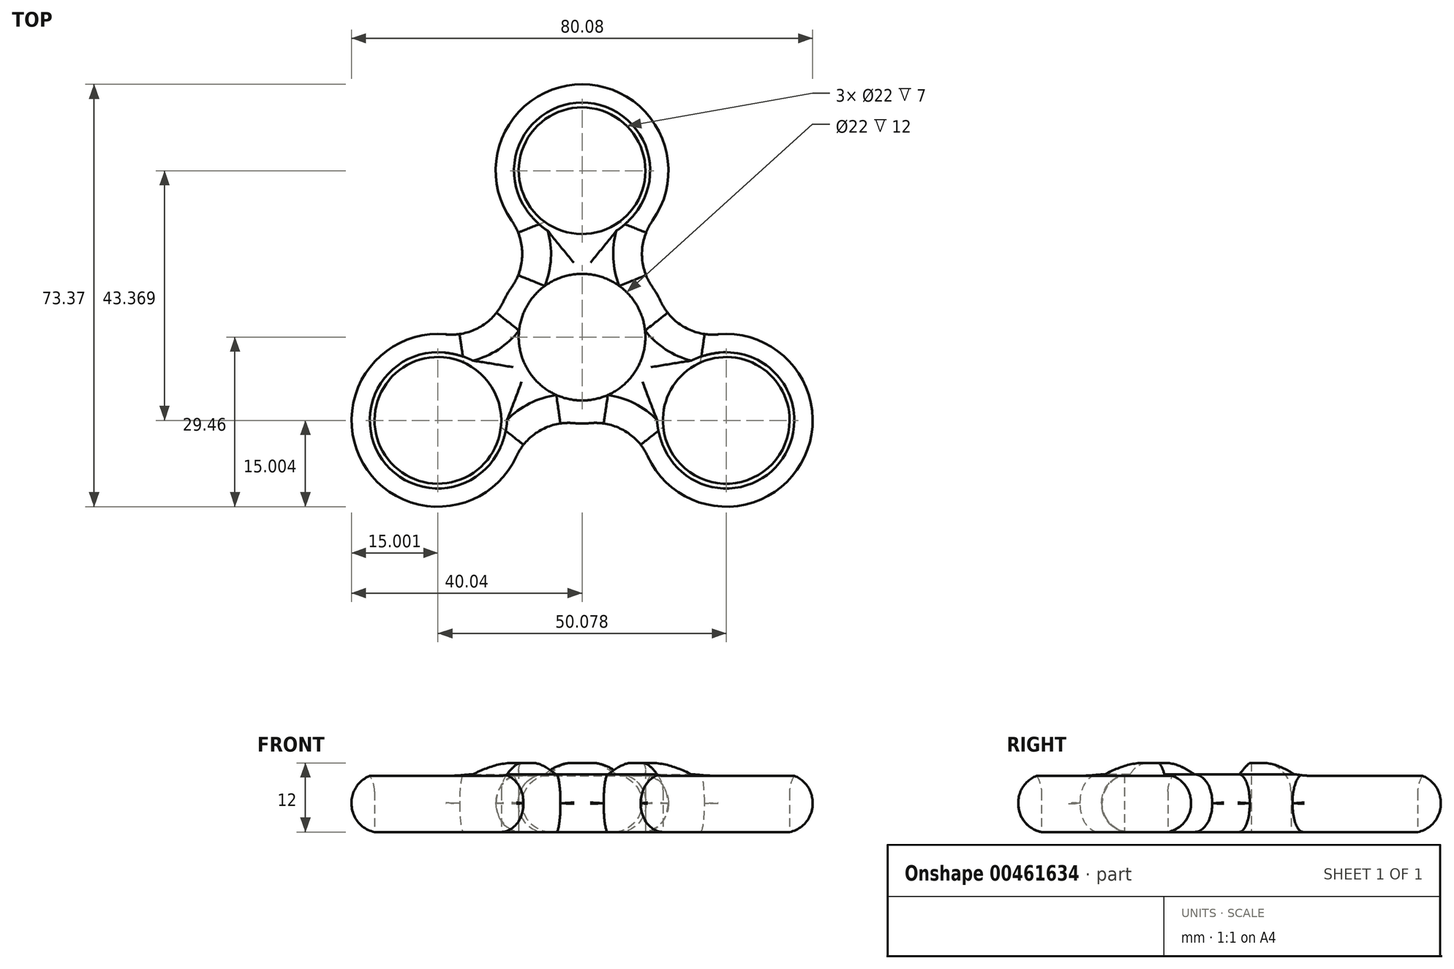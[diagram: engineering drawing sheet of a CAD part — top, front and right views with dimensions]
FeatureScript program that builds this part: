
annotation { "Feature Type Name" : "Feature", "Feature Type Description" : "" }
export const myFeature = defineFeature(function(context is Context, id is Id, definition is map)
    precondition{}
    {
        {
            var Q0;
            Q0=qCreatedBy(makeId("Top.planeOp"),FACE);
            var sketch = newSketch(context, id + "F0", { "sketchPlane" : qUnion([Q0])});
            skCircle(sketch, "E0", {"center": v(0, 0) * mm, "radius": 15 * mm});
            skSolve(sketch);
        }
        {
            var Q0;
            Q0=makeQuery(id+"FH3G6jVPPzJaUqX_0.imprint","IMPRINT",FACE,{"disambiguationData":[TD([[makeQuery(id+"FH3G6jVPPzJaUqX_0.imprint","IMPRINT",EDGE,{"derivedFrom":sQuery(id+"FH3G6jVPPzJaUqX_0.wireOp",EDGE,"1t66u0ux-Mq9E-4tRe-va77-gWhJsKDot20C")}),1.0]])]});
            var Q1;
            Q1=makeQuery(id+"F0.imprint","IMPRINT",FACE,{"disambiguationData":[TD([[makeQuery(id+"F0.imprint","IMPRINT",EDGE,{"derivedFrom":sQuery(id+"F0.wireOp",EDGE,"E0")}),1.0]])]});
            var Q2;
            Q2=makeQuery(id+"FH3G6jVPPzJaUqX_0.imprint","IMPRINT",FACE,{"disambiguationData":[TD([[makeQuery(id+"FH3G6jVPPzJaUqX_0.imprint","IMPRINT",EDGE,{"derivedFrom":sQuery(id+"FH3G6jVPPzJaUqX_0.wireOp",EDGE,"5f4d2418-c4b2-435b-843a-2def000c6f27.2.0")}),1.0]])]});
            var Q3;
            Q3=makeQuery(id+"FH3G6jVPPzJaUqX_0.imprint","IMPRINT",FACE,{"disambiguationData":[TD([[makeQuery(id+"FH3G6jVPPzJaUqX_0.imprint","IMPRINT",EDGE,{"derivedFrom":sQuery(id+"FH3G6jVPPzJaUqX_0.wireOp",EDGE,"5f4d2418-c4b2-435b-843a-2def000c6f27.1.0")}),1.0]])]});
            extrude(context, id + "F1", {"entities" : qUnion([Q0, Q1, Q2, Q3]), "depth" : 10 * mm, "offsetDistance" : 25 * mm});
        }
        {
            var Q0;
            Q0=qCreatedBy(makeId("Top.planeOp"),FACE);
            var sketch = newSketch(context, id + "F2", { "sketchPlane" : qUnion([Q0])});
            skCircle(sketch, "E1", {"center": v(0, 28.91) * mm, "radius": 15 * mm});
            skCircle(sketch, "E2.1.0", {"center": v(-25.04, -14.46) * mm, "radius": 15 * mm});
            skCircle(sketch, "E2.2.0", {"center": v(25.04, -14.46) * mm, "radius": 15 * mm});
            skPoint(sketch, "E2.center", {"position": v(0, 0) * mm});
            skSolve(sketch);
        }
        {
            var Q0;
            Q0=makeQuery(id+"F2.imprint","IMPRINT",FACE,{"disambiguationData":[TD([[makeQuery(id+"F2.imprint","IMPRINT",EDGE,{"derivedFrom":sQuery(id+"F2.wireOp",EDGE,"E1")}),1.0]])]});
            var Q1;
            Q1=makeQuery(id+"F2.imprint","IMPRINT",FACE,{"disambiguationData":[TD([[makeQuery(id+"F2.imprint","IMPRINT",EDGE,{"derivedFrom":sQuery(id+"F2.wireOp",EDGE,"E2.2.0")}),1.0]])]});
            var Q2;
            Q2=makeQuery(id+"F2.imprint","IMPRINT",FACE,{"disambiguationData":[TD([[makeQuery(id+"F2.imprint","IMPRINT",EDGE,{"derivedFrom":sQuery(id+"F2.wireOp",EDGE,"E2.1.0")}),1.0]])]});
            extrude(context, id + "F3", {"entities" : qUnion([Q0, Q1, Q2]), "operationType" : NewBodyOperationType.ADD, "depth" : 10 * mm, "offsetDistance" : 25 * mm});
        }
        {
            var Q0;
            Q0=makeQuery(id+"F3.boolean.opBoolean","MERGE",FACE,{"derivedFrom":[makeQuery(id+"F1.opExtrude","CAP_FACE",FACE,{"disambiguationData":[OSD([sQuery(id+"F0.wireOp",EDGE,"E0")])],"isStart":true}),makeQuery(id+"F3.opExtrude","CAP_FACE",FACE,{"disambiguationData":[OSD([sQuery(id+"F2.wireOp",EDGE,"E1")])],"isStart":true}),makeQuery(id+"F3.opExtrude","CAP_FACE",FACE,{"disambiguationData":[OSD([sQuery(id+"F2.wireOp",EDGE,"E2.1.0")])],"isStart":true}),makeQuery(id+"F3.opExtrude","CAP_FACE",FACE,{"disambiguationData":[OSD([sQuery(id+"F2.wireOp",EDGE,"E2.2.0")])],"isStart":true})]});
            var sketch = newSketch(context, id + "F4", { "sketchPlane" : qUnion([Q0])});
            skCircle(sketch, "E3", {"center": v(0, -28.91) * mm, "radius": 11 * mm});
            skSolve(sketch);
        }
        {
            var Q0;
            Q0=makeQuery(id+"F4.imprint","IMPRINT",FACE,{"disambiguationData":[TD([[makeQuery(id+"F4.imprint","IMPRINT",EDGE,{"derivedFrom":sQuery(id+"F4.wireOp",EDGE,"E3")}),-1.0]])]});
            var sketch = newSketch(context, id + "F5", { "sketchPlane" : qUnion([Q0])});
            skCircle(sketch, "E4", {"center": v(0, 0) * mm, "radius": 11 * mm});
            skSolve(sketch);
        }
        {
            var Q0;
            Q0=makeQuery(id+"F4.imprint","IMPRINT",FACE,{"disambiguationData":[TD([[makeQuery(id+"F4.imprint","IMPRINT",EDGE,{"derivedFrom":sQuery(id+"F4.wireOp",EDGE,"E3")}),1.0]])]});
            extrude(context, id + "F6", {"entities" : qUnion([Q0]), "operationType" : NewBodyOperationType.REMOVE, "oppositeDirection" : true, "depth" : 25 * mm, "offsetDistance" : 25 * mm});
        }
        {
            var Q0;
            Q0=makeQuery(id+"F5.imprint","IMPRINT",FACE,{"disambiguationData":[TD([[makeQuery(id+"F5.imprint","IMPRINT",EDGE,{"derivedFrom":sQuery(id+"F5.wireOp",EDGE,"E4")}),1.0]])]});
            extrude(context, id + "F7", {"entities" : qUnion([Q0]), "operationType" : NewBodyOperationType.REMOVE, "oppositeDirection" : true, "depth" : 25 * mm, "offsetDistance" : 25 * mm});
        }
        {
            var Q0;
            Q0=makeQuery(id+"F3.boolean.opBoolean","MERGE",FACE,{"derivedFrom":[makeQuery(id+"F1.opExtrude","CAP_FACE",FACE,{"disambiguationData":[OSD([sQuery(id+"F0.wireOp",EDGE,"E0")])],"isStart":true}),makeQuery(id+"F3.opExtrude","CAP_FACE",FACE,{"disambiguationData":[OSD([sQuery(id+"F2.wireOp",EDGE,"E1")])],"isStart":true}),makeQuery(id+"F3.opExtrude","CAP_FACE",FACE,{"disambiguationData":[OSD([sQuery(id+"F2.wireOp",EDGE,"E2.1.0")])],"isStart":true}),makeQuery(id+"F3.opExtrude","CAP_FACE",FACE,{"disambiguationData":[OSD([sQuery(id+"F2.wireOp",EDGE,"E2.2.0")])],"isStart":true})]});
            var sketch = newSketch(context, id + "F8", { "sketchPlane" : qUnion([Q0])});
            skCircle(sketch, "E5", {"center": v(-25.04, 14.46) * mm, "radius": 11 * mm});
            skSolve(sketch);
        }
        {
            var Q0;
            Q0=makeQuery(id+"F8.imprint","IMPRINT",FACE,{"disambiguationData":[TD([[makeQuery(id+"F8.imprint","IMPRINT",EDGE,{"derivedFrom":sQuery(id+"F8.wireOp",EDGE,"E5")}),1.0]])]});
            extrude(context, id + "F9", {"entities" : qUnion([Q0]), "operationType" : NewBodyOperationType.REMOVE, "oppositeDirection" : true, "depth" : 25 * mm, "offsetDistance" : 25 * mm});
        }
        {
            var Q0;
            Q0=makeQuery(id+"F3.boolean.opBoolean","MERGE",FACE,{"derivedFrom":[makeQuery(id+"F1.opExtrude","CAP_FACE",FACE,{"disambiguationData":[OSD([sQuery(id+"F0.wireOp",EDGE,"E0")])],"isStart":true}),makeQuery(id+"F3.opExtrude","CAP_FACE",FACE,{"disambiguationData":[OSD([sQuery(id+"F2.wireOp",EDGE,"E1")])],"isStart":true}),makeQuery(id+"F3.opExtrude","CAP_FACE",FACE,{"disambiguationData":[OSD([sQuery(id+"F2.wireOp",EDGE,"E2.1.0")])],"isStart":true}),makeQuery(id+"F3.opExtrude","CAP_FACE",FACE,{"disambiguationData":[OSD([sQuery(id+"F2.wireOp",EDGE,"E2.2.0")])],"isStart":true})]});
            var sketch = newSketch(context, id + "F10", { "sketchPlane" : qUnion([Q0])});
            skCircle(sketch, "E6", {"center": v(25.04, 14.46) * mm, "radius": 11 * mm});
            skSolve(sketch);
        }
        {
            var Q0;
            Q0=makeQuery(id+"F10.imprint","IMPRINT",FACE,{"disambiguationData":[TD([[makeQuery(id+"F10.imprint","IMPRINT",EDGE,{"derivedFrom":sQuery(id+"F10.wireOp",EDGE,"E6")}),1.0]])]});
            extrude(context, id + "F11", {"entities" : qUnion([Q0]), "operationType" : NewBodyOperationType.REMOVE, "oppositeDirection" : true, "depth" : 25 * mm, "offsetDistance" : 25 * mm});
        }
        {
            var Q0;
            Q0=makeQuery(id+"F3.boolean.opBoolean","INTERSECT",EDGE,{"disambiguationData":[OD(1.0)],"derivedFrom":[makeQuery(id+"F1.opExtrude","SWEPT_FACE",FACE,{"disambiguationData":[OSD([sQuery(id+"F0.wireOp",EDGE,"E0")])]}),makeQuery(id+"F3.opExtrude","SWEPT_FACE",FACE,{"disambiguationData":[OSD([sQuery(id+"F2.wireOp",EDGE,"E2.2.0")])]})]});
            var Q1;
            Q1=makeQuery(id+"F3.boolean.opBoolean","INTERSECT",EDGE,{"disambiguationData":[OD(1.0)],"derivedFrom":[makeQuery(id+"F1.opExtrude","SWEPT_FACE",FACE,{"disambiguationData":[OSD([sQuery(id+"F0.wireOp",EDGE,"E0")])]}),makeQuery(id+"F3.opExtrude","SWEPT_FACE",FACE,{"disambiguationData":[OSD([sQuery(id+"F2.wireOp",EDGE,"E2.1.0")])]})]});
            var Q2;
            Q2=makeQuery(id+"F3.boolean.opBoolean","INTERSECT",EDGE,{"disambiguationData":[OD(0.0)],"derivedFrom":[makeQuery(id+"F1.opExtrude","SWEPT_FACE",FACE,{"disambiguationData":[OSD([sQuery(id+"F0.wireOp",EDGE,"E0")])]}),makeQuery(id+"F3.opExtrude","SWEPT_FACE",FACE,{"disambiguationData":[OSD([sQuery(id+"F2.wireOp",EDGE,"E2.1.0")])]})]});
            var Q3;
            Q3=makeQuery(id+"F3.boolean.opBoolean","INTERSECT",EDGE,{"disambiguationData":[OD(0.0)],"derivedFrom":[makeQuery(id+"F1.opExtrude","SWEPT_FACE",FACE,{"disambiguationData":[OSD([sQuery(id+"F0.wireOp",EDGE,"E0")])]}),makeQuery(id+"F3.opExtrude","SWEPT_FACE",FACE,{"disambiguationData":[OSD([sQuery(id+"F2.wireOp",EDGE,"E1")])]})]});
            var Q4;
            Q4=makeQuery(id+"F3.boolean.opBoolean","INTERSECT",EDGE,{"disambiguationData":[OD(1.0)],"derivedFrom":[makeQuery(id+"F1.opExtrude","SWEPT_FACE",FACE,{"disambiguationData":[OSD([sQuery(id+"F0.wireOp",EDGE,"E0")])]}),makeQuery(id+"F3.opExtrude","SWEPT_FACE",FACE,{"disambiguationData":[OSD([sQuery(id+"F2.wireOp",EDGE,"E1")])]})]});
            var Q5;
            Q5=makeQuery(id+"F3.boolean.opBoolean","INTERSECT",EDGE,{"disambiguationData":[OD(0.0)],"derivedFrom":[makeQuery(id+"F1.opExtrude","SWEPT_FACE",FACE,{"disambiguationData":[OSD([sQuery(id+"F0.wireOp",EDGE,"E0")])]}),makeQuery(id+"F3.opExtrude","SWEPT_FACE",FACE,{"disambiguationData":[OSD([sQuery(id+"F2.wireOp",EDGE,"E2.2.0")])]})]});
            fillet(context, id + "F12", {"entities" : qUnion([Q0, Q1, Q2, Q3, Q4, Q5]), "radius" : 10 * mm, "tangentPropagation" : true, "allowEdgeOverflow" : false});
        }
        {
            var Q0;
            Q0=makeQuery(id+"F3.opExtrude","CAP_EDGE",EDGE,{"disambiguationData":[OSD([sQuery(id+"F2.wireOp",EDGE,"E2.1.0")])],"isStart":true});
            var Q1;
            Q1=makeQuery(id+"F3.opExtrude","CAP_EDGE",EDGE,{"disambiguationData":[OSD([sQuery(id+"F2.wireOp",EDGE,"E1")])],"isStart":false});
            fillet(context, id + "F13", {"entities" : qUnion([Q0, Q1]), "radius" : 5 * mm, "tangentPropagation" : true, "allowEdgeOverflow" : false});
        }
        {
            var Q0;
            Q0=makeQuery(id+"F13.opFillet","SPLIT",FACE,{"disambiguationData":[OD(2.0)],"derivedFrom":makeQuery(id+"F3.boolean.opBoolean","MERGE",FACE,{"derivedFrom":[makeQuery(id+"F1.opExtrude","CAP_FACE",FACE,{"disambiguationData":[OSD([sQuery(id+"F0.wireOp",EDGE,"E0")])],"isStart":false}),makeQuery(id+"F3.opExtrude","CAP_FACE",FACE,{"disambiguationData":[OSD([sQuery(id+"F2.wireOp",EDGE,"E1")])],"isStart":false}),makeQuery(id+"F3.opExtrude","CAP_FACE",FACE,{"disambiguationData":[OSD([sQuery(id+"F2.wireOp",EDGE,"E2.1.0")])],"isStart":false}),makeQuery(id+"F3.opExtrude","CAP_FACE",FACE,{"disambiguationData":[OSD([sQuery(id+"F2.wireOp",EDGE,"E2.2.0")])],"isStart":false})]})});
            extrude(context, id + "F14", {"entities" : qUnion([Q0]), "operationType" : NewBodyOperationType.ADD, "depth" : 2 * mm, "offsetDistance" : 25 * mm});
        }
        {
            var Q0;
            Q0=makeQuery(id+"F13.opFillet","SPLIT",FACE,{"disambiguationData":[OD(0.0)],"derivedFrom":makeQuery(id+"F3.boolean.opBoolean","MERGE",FACE,{"derivedFrom":[makeQuery(id+"F1.opExtrude","CAP_FACE",FACE,{"disambiguationData":[OSD([sQuery(id+"F0.wireOp",EDGE,"E0")])],"isStart":false}),makeQuery(id+"F3.opExtrude","CAP_FACE",FACE,{"disambiguationData":[OSD([sQuery(id+"F2.wireOp",EDGE,"E1")])],"isStart":false}),makeQuery(id+"F3.opExtrude","CAP_FACE",FACE,{"disambiguationData":[OSD([sQuery(id+"F2.wireOp",EDGE,"E2.1.0")])],"isStart":false}),makeQuery(id+"F3.opExtrude","CAP_FACE",FACE,{"disambiguationData":[OSD([sQuery(id+"F2.wireOp",EDGE,"E2.2.0")])],"isStart":false})]})});
            var Q1;
            Q1=makeQuery(id+"F13.opFillet","SPLIT",FACE,{"disambiguationData":[OD(1.0)],"derivedFrom":makeQuery(id+"F3.boolean.opBoolean","MERGE",FACE,{"derivedFrom":[makeQuery(id+"F1.opExtrude","CAP_FACE",FACE,{"disambiguationData":[OSD([sQuery(id+"F0.wireOp",EDGE,"E0")])],"isStart":false}),makeQuery(id+"F3.opExtrude","CAP_FACE",FACE,{"disambiguationData":[OSD([sQuery(id+"F2.wireOp",EDGE,"E1")])],"isStart":false}),makeQuery(id+"F3.opExtrude","CAP_FACE",FACE,{"disambiguationData":[OSD([sQuery(id+"F2.wireOp",EDGE,"E2.1.0")])],"isStart":false}),makeQuery(id+"F3.opExtrude","CAP_FACE",FACE,{"disambiguationData":[OSD([sQuery(id+"F2.wireOp",EDGE,"E2.2.0")])],"isStart":false})]})});
            extrude(context, id + "F15", {"entities" : qUnion([Q0, Q1]), "operationType" : NewBodyOperationType.ADD, "depth" : 2 * mm, "offsetDistance" : 25 * mm});
        }
        {
            var Q0;
            Q0=makeQuery(id+"F15.opExtrude","CAP_EDGE",EDGE,{"disambiguationData":[OSD([sQuery(id+"F0.wireOp",EDGE,"E0"),sQuery(id+"F2.wireOp",EDGE,"E1"),sQuery(id+"F2.wireOp",EDGE,"E2.1.0"),sQuery(id+"F2.wireOp",EDGE,"E2.2.0"),sQuery(id+"F8.wireOp",EDGE,"E5")])],"isStart":false});
            var Q1;
            Q1=makeQuery(id+"F14.opExtrude","CAP_EDGE",EDGE,{"disambiguationData":[OSD([sQuery(id+"F0.wireOp",EDGE,"E0"),sQuery(id+"F2.wireOp",EDGE,"E1"),sQuery(id+"F2.wireOp",EDGE,"E2.1.0"),sQuery(id+"F2.wireOp",EDGE,"E2.2.0"),sQuery(id+"F10.wireOp",EDGE,"E6")])],"isStart":false});
            var Q2;
            Q2=makeQuery(id+"F15.opExtrude","CAP_EDGE",EDGE,{"disambiguationData":[OSD([sQuery(id+"F0.wireOp",EDGE,"E0"),sQuery(id+"F2.wireOp",EDGE,"E1"),sQuery(id+"F2.wireOp",EDGE,"E2.1.0"),sQuery(id+"F2.wireOp",EDGE,"E2.2.0"),sQuery(id+"F4.wireOp",EDGE,"E3")])],"isStart":false});
            fillet(context, id + "F16", {"entities" : qUnion([Q0, Q1, Q2]), "radius" : 5 * mm, "tangentPropagation" : true, "allowEdgeOverflow" : false});
        }
        {
            var Q0;
            {var subQ0=sQuery(id+"F2.wireOp",EDGE,"E2.2.0");var subQ1=sQuery(id+"F2.wireOp",EDGE,"E2.1.0");var subQ2=sQuery(id+"F2.wireOp",EDGE,"E1");var subQ3=sQuery(id+"F0.wireOp",EDGE,"E0");var subQ4=makeQuery(id+"F3.boolean.opBoolean","MERGE",FACE,{"derivedFrom":[makeQuery(id+"F1.opExtrude","CAP_FACE",FACE,{"disambiguationData":[OSD([subQ3])],"isStart":false}),makeQuery(id+"F3.opExtrude","CAP_FACE",FACE,{"disambiguationData":[OSD([subQ2])],"isStart":false}),makeQuery(id+"F3.opExtrude","CAP_FACE",FACE,{"disambiguationData":[OSD([subQ1])],"isStart":false}),makeQuery(id+"F3.opExtrude","CAP_FACE",FACE,{"disambiguationData":[OSD([subQ0])],"isStart":false})]});Q0=makeQuery(id+"F16.opFillet","BLEND_EDGE",EDGE,{"blendedFrom":[makeQuery(id+"F15.opExtrude","CAP_EDGE",EDGE,{"disambiguationData":[OSD([subQ3,subQ2,subQ1,subQ0,sQuery(id+"F8.wireOp",EDGE,"E5")])],"isStart":false}),makeQuery(id+"F15.opExtrude","SWEPT_FACE",FACE,{"disambiguationData":[OSD([subQ3,subQ2,subQ1,subQ0]),TDD([makeQuery(id+"F13.opFillet","BLEND_EDGE",EDGE,{"blendedFrom":[makeQuery(id+"F12.opFillet","BLEND_EDGE",EDGE,{"blendedFrom":[makeQuery(id+"F3.boolean.opBoolean","INTERSECT",EDGE,{"disambiguationData":[OD(0.0)],"derivedFrom":[makeQuery(id+"F1.opExtrude","SWEPT_FACE",FACE,{"disambiguationData":[OSD([subQ3])]}),makeQuery(id+"F3.opExtrude","SWEPT_FACE",FACE,{"disambiguationData":[OSD([subQ1])]})]}),subQ4],"blendedInto":[subQ4]}),subQ4],"blendedInto":[subQ4]})])]})],"blendedInto":[makeQuery(id+"F15.opExtrude","SWEPT_FACE",FACE,{"disambiguationData":[OSD([subQ3,subQ2,subQ1,subQ0]),TDD([makeQuery(id+"F13.opFillet","BLEND_EDGE",EDGE,{"blendedFrom":[makeQuery(id+"F12.opFillet","BLEND_EDGE",EDGE,{"blendedFrom":[makeQuery(id+"F3.boolean.opBoolean","INTERSECT",EDGE,{"disambiguationData":[OD(0.0)],"derivedFrom":[makeQuery(id+"F1.opExtrude","SWEPT_FACE",FACE,{"disambiguationData":[OSD([subQ3])]}),makeQuery(id+"F3.opExtrude","SWEPT_FACE",FACE,{"disambiguationData":[OSD([subQ1])]})]}),subQ4],"blendedInto":[subQ4]}),subQ4],"blendedInto":[subQ4]})])]})]});}
            fillet(context, id + "F17", {"entities" : qUnion([Q0]), "radius" : 5 * mm, "tangentPropagation" : true, "allowEdgeOverflow" : false});
        }
        {
            var Q0;
            {var subQ0=sQuery(id+"F2.wireOp",EDGE,"E2.2.0");var subQ1=sQuery(id+"F2.wireOp",EDGE,"E2.1.0");var subQ2=sQuery(id+"F2.wireOp",EDGE,"E1");var subQ3=sQuery(id+"F0.wireOp",EDGE,"E0");var subQ4=makeQuery(id+"F3.boolean.opBoolean","MERGE",FACE,{"derivedFrom":[makeQuery(id+"F1.opExtrude","CAP_FACE",FACE,{"disambiguationData":[OSD([subQ3])],"isStart":false}),makeQuery(id+"F3.opExtrude","CAP_FACE",FACE,{"disambiguationData":[OSD([subQ2])],"isStart":false}),makeQuery(id+"F3.opExtrude","CAP_FACE",FACE,{"disambiguationData":[OSD([subQ1])],"isStart":false}),makeQuery(id+"F3.opExtrude","CAP_FACE",FACE,{"disambiguationData":[OSD([subQ0])],"isStart":false})]});Q0=makeQuery(id+"F16.opFillet","BLEND_EDGE",EDGE,{"blendedFrom":[makeQuery(id+"F15.opExtrude","CAP_EDGE",EDGE,{"disambiguationData":[OSD([subQ3,subQ2,subQ1,subQ0,sQuery(id+"F8.wireOp",EDGE,"E5")])],"isStart":false}),makeQuery(id+"F15.opExtrude","SWEPT_FACE",FACE,{"disambiguationData":[OSD([subQ3,subQ2,subQ1,subQ0]),TDD([makeQuery(id+"F13.opFillet","BLEND_EDGE",EDGE,{"blendedFrom":[makeQuery(id+"F12.opFillet","BLEND_EDGE",EDGE,{"blendedFrom":[makeQuery(id+"F3.boolean.opBoolean","INTERSECT",EDGE,{"disambiguationData":[OD(1.0)],"derivedFrom":[makeQuery(id+"F1.opExtrude","SWEPT_FACE",FACE,{"disambiguationData":[OSD([subQ3])]}),makeQuery(id+"F3.opExtrude","SWEPT_FACE",FACE,{"disambiguationData":[OSD([subQ1])]})]}),subQ4],"blendedInto":[subQ4]}),subQ4],"blendedInto":[subQ4]})])]})],"blendedInto":[makeQuery(id+"F15.opExtrude","SWEPT_FACE",FACE,{"disambiguationData":[OSD([subQ3,subQ2,subQ1,subQ0]),TDD([makeQuery(id+"F13.opFillet","BLEND_EDGE",EDGE,{"blendedFrom":[makeQuery(id+"F12.opFillet","BLEND_EDGE",EDGE,{"blendedFrom":[makeQuery(id+"F3.boolean.opBoolean","INTERSECT",EDGE,{"disambiguationData":[OD(1.0)],"derivedFrom":[makeQuery(id+"F1.opExtrude","SWEPT_FACE",FACE,{"disambiguationData":[OSD([subQ3])]}),makeQuery(id+"F3.opExtrude","SWEPT_FACE",FACE,{"disambiguationData":[OSD([subQ1])]})]}),subQ4],"blendedInto":[subQ4]}),subQ4],"blendedInto":[subQ4]})])]})]});}
            fillet(context, id + "F18", {"entities" : qUnion([Q0]), "radius" : 5 * mm, "tangentPropagation" : true, "allowEdgeOverflow" : false});
        }
        {
            var Q0;
            {var subQ0=sQuery(id+"F2.wireOp",EDGE,"E2.2.0");var subQ1=sQuery(id+"F2.wireOp",EDGE,"E2.1.0");var subQ2=sQuery(id+"F2.wireOp",EDGE,"E1");var subQ3=sQuery(id+"F0.wireOp",EDGE,"E0");var subQ4=makeQuery(id+"F3.boolean.opBoolean","MERGE",FACE,{"derivedFrom":[makeQuery(id+"F1.opExtrude","CAP_FACE",FACE,{"disambiguationData":[OSD([subQ3])],"isStart":false}),makeQuery(id+"F3.opExtrude","CAP_FACE",FACE,{"disambiguationData":[OSD([subQ2])],"isStart":false}),makeQuery(id+"F3.opExtrude","CAP_FACE",FACE,{"disambiguationData":[OSD([subQ1])],"isStart":false}),makeQuery(id+"F3.opExtrude","CAP_FACE",FACE,{"disambiguationData":[OSD([subQ0])],"isStart":false})]});Q0=makeQuery(id+"F16.opFillet","BLEND_EDGE",EDGE,{"blendedFrom":[makeQuery(id+"F14.opExtrude","CAP_EDGE",EDGE,{"disambiguationData":[OSD([subQ3,subQ2,subQ1,subQ0,sQuery(id+"F10.wireOp",EDGE,"E6")])],"isStart":false}),makeQuery(id+"F14.opExtrude","SWEPT_FACE",FACE,{"disambiguationData":[OSD([subQ3,subQ2,subQ1,subQ0]),TDD([makeQuery(id+"F13.opFillet","BLEND_EDGE",EDGE,{"blendedFrom":[makeQuery(id+"F12.opFillet","BLEND_EDGE",EDGE,{"blendedFrom":[makeQuery(id+"F3.boolean.opBoolean","INTERSECT",EDGE,{"disambiguationData":[OD(0.0)],"derivedFrom":[makeQuery(id+"F1.opExtrude","SWEPT_FACE",FACE,{"disambiguationData":[OSD([subQ3])]}),makeQuery(id+"F3.opExtrude","SWEPT_FACE",FACE,{"disambiguationData":[OSD([subQ0])]})]}),subQ4],"blendedInto":[subQ4]}),subQ4],"blendedInto":[subQ4]})])]})],"blendedInto":[makeQuery(id+"F14.opExtrude","SWEPT_FACE",FACE,{"disambiguationData":[OSD([subQ3,subQ2,subQ1,subQ0]),TDD([makeQuery(id+"F13.opFillet","BLEND_EDGE",EDGE,{"blendedFrom":[makeQuery(id+"F12.opFillet","BLEND_EDGE",EDGE,{"blendedFrom":[makeQuery(id+"F3.boolean.opBoolean","INTERSECT",EDGE,{"disambiguationData":[OD(0.0)],"derivedFrom":[makeQuery(id+"F1.opExtrude","SWEPT_FACE",FACE,{"disambiguationData":[OSD([subQ3])]}),makeQuery(id+"F3.opExtrude","SWEPT_FACE",FACE,{"disambiguationData":[OSD([subQ0])]})]}),subQ4],"blendedInto":[subQ4]}),subQ4],"blendedInto":[subQ4]})])]})]});}
            fillet(context, id + "F19", {"entities" : qUnion([Q0]), "radius" : 5 * mm, "tangentPropagation" : true, "allowEdgeOverflow" : false});
        }
        {
            var Q0;
            {var subQ0=sQuery(id+"F2.wireOp",EDGE,"E2.2.0");var subQ1=sQuery(id+"F2.wireOp",EDGE,"E2.1.0");var subQ2=sQuery(id+"F2.wireOp",EDGE,"E1");var subQ3=sQuery(id+"F0.wireOp",EDGE,"E0");var subQ4=makeQuery(id+"F3.boolean.opBoolean","MERGE",FACE,{"derivedFrom":[makeQuery(id+"F1.opExtrude","CAP_FACE",FACE,{"disambiguationData":[OSD([subQ3])],"isStart":false}),makeQuery(id+"F3.opExtrude","CAP_FACE",FACE,{"disambiguationData":[OSD([subQ2])],"isStart":false}),makeQuery(id+"F3.opExtrude","CAP_FACE",FACE,{"disambiguationData":[OSD([subQ1])],"isStart":false}),makeQuery(id+"F3.opExtrude","CAP_FACE",FACE,{"disambiguationData":[OSD([subQ0])],"isStart":false})]});Q0=makeQuery(id+"F16.opFillet","BLEND_EDGE",EDGE,{"blendedFrom":[makeQuery(id+"F14.opExtrude","CAP_EDGE",EDGE,{"disambiguationData":[OSD([subQ3,subQ2,subQ1,subQ0,sQuery(id+"F10.wireOp",EDGE,"E6")])],"isStart":false}),makeQuery(id+"F14.opExtrude","SWEPT_FACE",FACE,{"disambiguationData":[OSD([subQ3,subQ2,subQ1,subQ0]),TDD([makeQuery(id+"F13.opFillet","BLEND_EDGE",EDGE,{"blendedFrom":[makeQuery(id+"F12.opFillet","BLEND_EDGE",EDGE,{"blendedFrom":[makeQuery(id+"F3.boolean.opBoolean","INTERSECT",EDGE,{"disambiguationData":[OD(1.0)],"derivedFrom":[makeQuery(id+"F1.opExtrude","SWEPT_FACE",FACE,{"disambiguationData":[OSD([subQ3])]}),makeQuery(id+"F3.opExtrude","SWEPT_FACE",FACE,{"disambiguationData":[OSD([subQ0])]})]}),subQ4],"blendedInto":[subQ4]}),subQ4],"blendedInto":[subQ4]})])]})],"blendedInto":[makeQuery(id+"F14.opExtrude","SWEPT_FACE",FACE,{"disambiguationData":[OSD([subQ3,subQ2,subQ1,subQ0]),TDD([makeQuery(id+"F13.opFillet","BLEND_EDGE",EDGE,{"blendedFrom":[makeQuery(id+"F12.opFillet","BLEND_EDGE",EDGE,{"blendedFrom":[makeQuery(id+"F3.boolean.opBoolean","INTERSECT",EDGE,{"disambiguationData":[OD(1.0)],"derivedFrom":[makeQuery(id+"F1.opExtrude","SWEPT_FACE",FACE,{"disambiguationData":[OSD([subQ3])]}),makeQuery(id+"F3.opExtrude","SWEPT_FACE",FACE,{"disambiguationData":[OSD([subQ0])]})]}),subQ4],"blendedInto":[subQ4]}),subQ4],"blendedInto":[subQ4]})])]})]});}
            fillet(context, id + "F20", {"entities" : qUnion([Q0]), "radius" : 5 * mm, "tangentPropagation" : true, "allowEdgeOverflow" : false});
        }
        {
            var Q0;
            {var subQ0=sQuery(id+"F2.wireOp",EDGE,"E2.2.0");var subQ1=sQuery(id+"F2.wireOp",EDGE,"E2.1.0");var subQ2=sQuery(id+"F2.wireOp",EDGE,"E1");var subQ3=sQuery(id+"F0.wireOp",EDGE,"E0");var subQ4=makeQuery(id+"F3.boolean.opBoolean","MERGE",FACE,{"derivedFrom":[makeQuery(id+"F1.opExtrude","CAP_FACE",FACE,{"disambiguationData":[OSD([subQ3])],"isStart":false}),makeQuery(id+"F3.opExtrude","CAP_FACE",FACE,{"disambiguationData":[OSD([subQ2])],"isStart":false}),makeQuery(id+"F3.opExtrude","CAP_FACE",FACE,{"disambiguationData":[OSD([subQ1])],"isStart":false}),makeQuery(id+"F3.opExtrude","CAP_FACE",FACE,{"disambiguationData":[OSD([subQ0])],"isStart":false})]});Q0=makeQuery(id+"F16.opFillet","BLEND_EDGE",EDGE,{"blendedFrom":[makeQuery(id+"F15.opExtrude","CAP_EDGE",EDGE,{"disambiguationData":[OSD([subQ3,subQ2,subQ1,subQ0,sQuery(id+"F4.wireOp",EDGE,"E3")])],"isStart":false}),makeQuery(id+"F15.opExtrude","SWEPT_FACE",FACE,{"disambiguationData":[OSD([subQ3,subQ2,subQ1,subQ0]),TDD([makeQuery(id+"F13.opFillet","BLEND_EDGE",EDGE,{"blendedFrom":[makeQuery(id+"F12.opFillet","BLEND_EDGE",EDGE,{"blendedFrom":[makeQuery(id+"F3.boolean.opBoolean","INTERSECT",EDGE,{"disambiguationData":[OD(0.0)],"derivedFrom":[makeQuery(id+"F1.opExtrude","SWEPT_FACE",FACE,{"disambiguationData":[OSD([subQ3])]}),makeQuery(id+"F3.opExtrude","SWEPT_FACE",FACE,{"disambiguationData":[OSD([subQ2])]})]}),subQ4],"blendedInto":[subQ4]}),subQ4],"blendedInto":[subQ4]})])]})],"blendedInto":[makeQuery(id+"F15.opExtrude","SWEPT_FACE",FACE,{"disambiguationData":[OSD([subQ3,subQ2,subQ1,subQ0]),TDD([makeQuery(id+"F13.opFillet","BLEND_EDGE",EDGE,{"blendedFrom":[makeQuery(id+"F12.opFillet","BLEND_EDGE",EDGE,{"blendedFrom":[makeQuery(id+"F3.boolean.opBoolean","INTERSECT",EDGE,{"disambiguationData":[OD(0.0)],"derivedFrom":[makeQuery(id+"F1.opExtrude","SWEPT_FACE",FACE,{"disambiguationData":[OSD([subQ3])]}),makeQuery(id+"F3.opExtrude","SWEPT_FACE",FACE,{"disambiguationData":[OSD([subQ2])]})]}),subQ4],"blendedInto":[subQ4]}),subQ4],"blendedInto":[subQ4]})])]})]});}
            var Q1;
            {var subQ0=sQuery(id+"F2.wireOp",EDGE,"E2.2.0");var subQ1=sQuery(id+"F2.wireOp",EDGE,"E2.1.0");var subQ2=sQuery(id+"F2.wireOp",EDGE,"E1");var subQ3=sQuery(id+"F0.wireOp",EDGE,"E0");var subQ4=makeQuery(id+"F3.boolean.opBoolean","MERGE",FACE,{"derivedFrom":[makeQuery(id+"F1.opExtrude","CAP_FACE",FACE,{"disambiguationData":[OSD([subQ3])],"isStart":false}),makeQuery(id+"F3.opExtrude","CAP_FACE",FACE,{"disambiguationData":[OSD([subQ2])],"isStart":false}),makeQuery(id+"F3.opExtrude","CAP_FACE",FACE,{"disambiguationData":[OSD([subQ1])],"isStart":false}),makeQuery(id+"F3.opExtrude","CAP_FACE",FACE,{"disambiguationData":[OSD([subQ0])],"isStart":false})]});Q1=makeQuery(id+"F16.opFillet","BLEND_EDGE",EDGE,{"blendedFrom":[makeQuery(id+"F15.opExtrude","CAP_EDGE",EDGE,{"disambiguationData":[OSD([subQ3,subQ2,subQ1,subQ0,sQuery(id+"F4.wireOp",EDGE,"E3")])],"isStart":false}),makeQuery(id+"F15.opExtrude","SWEPT_FACE",FACE,{"disambiguationData":[OSD([subQ3,subQ2,subQ1,subQ0]),TDD([makeQuery(id+"F13.opFillet","BLEND_EDGE",EDGE,{"blendedFrom":[makeQuery(id+"F12.opFillet","BLEND_EDGE",EDGE,{"blendedFrom":[makeQuery(id+"F3.boolean.opBoolean","INTERSECT",EDGE,{"disambiguationData":[OD(1.0)],"derivedFrom":[makeQuery(id+"F1.opExtrude","SWEPT_FACE",FACE,{"disambiguationData":[OSD([subQ3])]}),makeQuery(id+"F3.opExtrude","SWEPT_FACE",FACE,{"disambiguationData":[OSD([subQ2])]})]}),subQ4],"blendedInto":[subQ4]}),subQ4],"blendedInto":[subQ4]})])]})],"blendedInto":[makeQuery(id+"F15.opExtrude","SWEPT_FACE",FACE,{"disambiguationData":[OSD([subQ3,subQ2,subQ1,subQ0]),TDD([makeQuery(id+"F13.opFillet","BLEND_EDGE",EDGE,{"blendedFrom":[makeQuery(id+"F12.opFillet","BLEND_EDGE",EDGE,{"blendedFrom":[makeQuery(id+"F3.boolean.opBoolean","INTERSECT",EDGE,{"disambiguationData":[OD(1.0)],"derivedFrom":[makeQuery(id+"F1.opExtrude","SWEPT_FACE",FACE,{"disambiguationData":[OSD([subQ3])]}),makeQuery(id+"F3.opExtrude","SWEPT_FACE",FACE,{"disambiguationData":[OSD([subQ2])]})]}),subQ4],"blendedInto":[subQ4]}),subQ4],"blendedInto":[subQ4]})])]})]});}
            fillet(context, id + "F21", {"entities" : qUnion([Q0, Q1]), "radius" : 5 * mm, "tangentPropagation" : true, "allowEdgeOverflow" : false});
        }
    });
